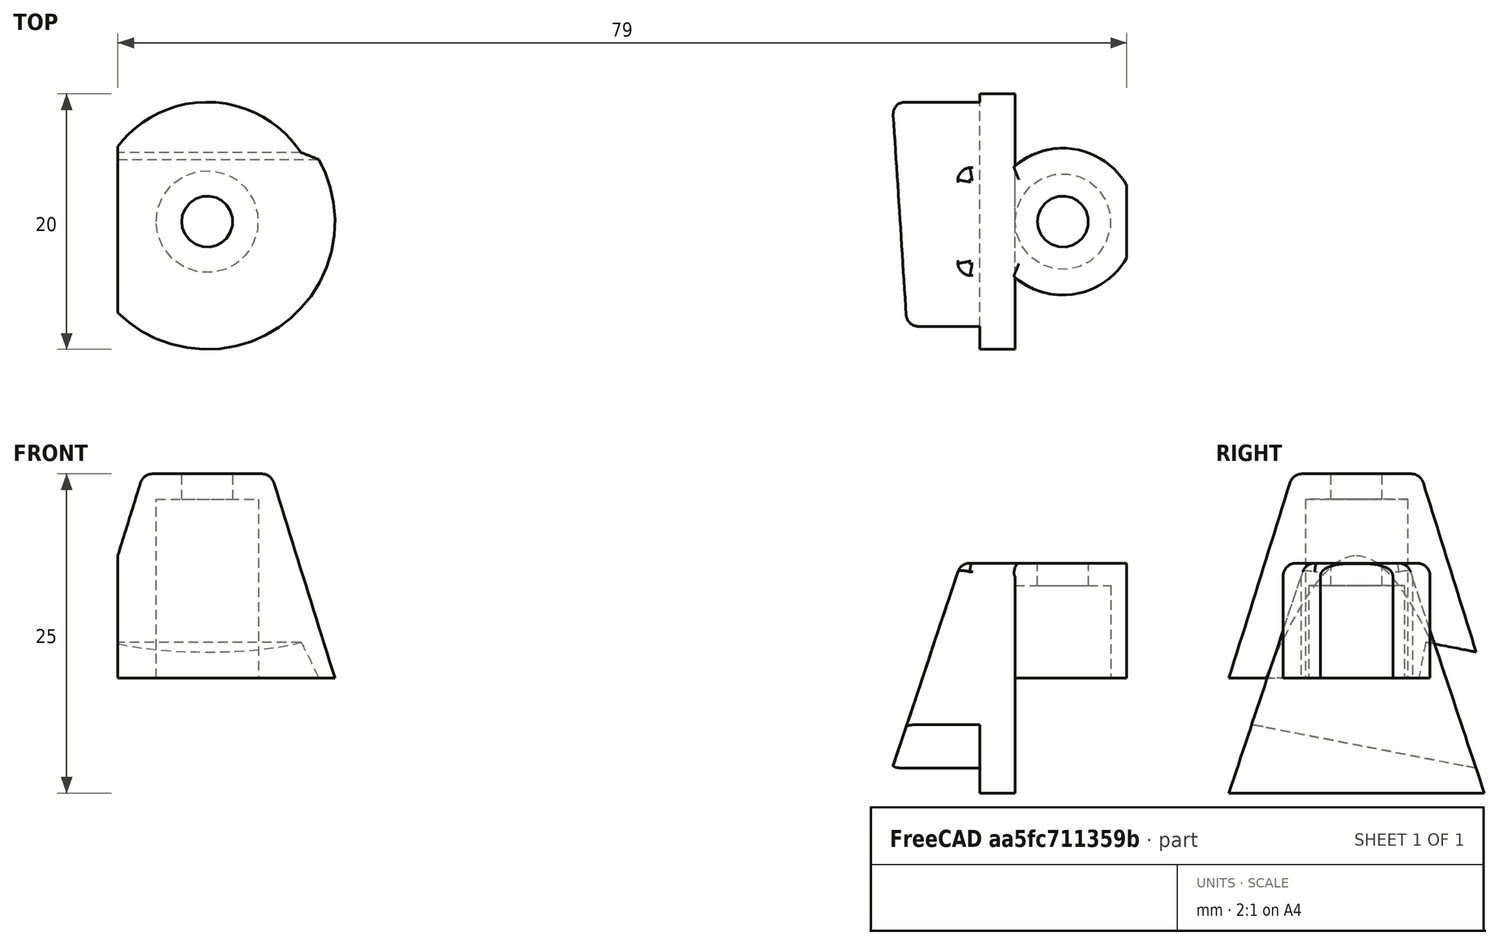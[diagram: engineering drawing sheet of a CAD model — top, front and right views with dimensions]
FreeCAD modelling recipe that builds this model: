
FCSTD DOCUMENT  (FreeCAD 0.21R33771 (Git))
Label: Decent800 brackets
License: All rights reserved
LicenseURL: http://en.wikipedia.org/wiki/All_rights_reserved
objects: PartDesign::SubtractiveCylinder×4, PartDesign::SubtractiveBox×4, PartDesign::Fillet×3, PartDesign::Body×2, Part::FeaturePython×2, PartDesign::AdditiveCylinder×1, PartDesign::AdditiveWedge×1, PartDesign::AdditiveCone×1, Spreadsheet::Sheet×1, PartDesign::Plane×1
note: 33 computed .brp shape members not serialized (recipe doc carries the construction recipe); baked Part::Feature solids carry a one-line shape summary decoded from their .brp

FEATURE [PartDesign::AdditiveCylinder] Cylinder
  Angle = 360
  AttacherType = Attacher::AttachEngine3D
  FirstAngle = 0
  Height = 9
  Radius = 5.75
  SecondAngle = 0
FEATURE [PartDesign::SubtractiveCylinder] Cylinder001
  Angle = 360
  AttacherType = Attacher::AttachEngine3D
  BaseFeature = -> Cylinder
  FirstAngle = 0
  Height = 9
  MapMode = 2
  Radius = 2
  SecondAngle = 0
  Support = -> [XY_Plane]
FEATURE [PartDesign::SubtractiveCylinder] Cylinder002
  Angle = 360
  AttacherType = Attacher::AttachEngine3D
  BaseFeature = -> Cylinder001
  FirstAngle = 0
  Height = 7.25
  MapMode = 5
  Radius = 3.75
  SecondAngle = 0
  Support = -> [XY_Plane]
FEATURE [PartDesign::AdditiveWedge] Wedge
  AttacherType = Attacher::AttachEngine3D
  BaseFeature = -> Cylinder002
  MapMode = 5
  Placement = pos=(0,0,0) rot=(0.57735,0.57735,0.57735;2.0944rad)
  Refine = true
  Support = -> [YZ_Plane]
  X2max = 4
  X2min = -4
  Xmax = 10
  Xmin = -10
  Ymax = 9
  Ymin = -9
  Z2max = 8
  Z2min = 3.75
  Zmax = 14
  Zmin = 3.75
FEATURE [PartDesign::SubtractiveBox] Box
  AttacherType = Attacher::AttachEngine3D
  AttachmentOffset = pos=(6.5,-15,-12.5) rot=(-1,0,0;0.191986rad)
  BaseFeature = -> Wedge
  Height = 10
  Length = 20
  MapMode = 5
  Placement = pos=(6.5,-15,-12.5) rot=(-1,0,0;0.191986rad)
  Support = -> [XY_Plane]
  Width = 30
  expr: .AttachmentOffset.Rotation.Angle = <<Spreadsheet>>.KeebAngle
FEATURE [PartDesign::Fillet] Fillet
  Base = -> Box [Edge8,Edge1]
  BaseFeature = -> Box
  Placement = pos=(6.5,-15,-12.5) rot=(-1,0,0;0.191986rad)
  Radius = 1
  SupportTransform = false
  UseAllEdges = false
FEATURE [PartDesign::Fillet] Fillet001
  Base = -> Fillet [Edge10,Edge9]
  BaseFeature = -> Fillet
  Placement = pos=(6.5,-15,-12.5) rot=(-1,0,0;0.191986rad)
  Radius = 1
  SupportTransform = false
  UseAllEdges = false
FEATURE [PartDesign::AdditiveCone] Cone
  Angle = 360
  AttacherType = Attacher::AttachEngine3D
  Height = 16
  MapMode = 5
  Radius1 = 10
  Radius2 = 5
  Support = -> [XY_Plane001]
FEATURE [PartDesign::SubtractiveCylinder] Cylinder003
  Angle = 360
  AttacherType = Attacher::AttachEngine3D
  BaseFeature = -> Cone
  FirstAngle = 0
  Height = 16
  MapMode = 2
  Radius = 2
  SecondAngle = 0
  Support = -> [Cylinder001]
FEATURE [PartDesign::SubtractiveCylinder] Cylinder004
  Angle = 360
  AttacherType = Attacher::AttachEngine3D
  BaseFeature = -> Cylinder003
  FirstAngle = 0
  Height = 14
  MapMode = 2
  Radius = 4
  SecondAngle = 0
  Support = -> [Cylinder002]
FEATURE [PartDesign::SubtractiveBox] Box001
  AttacherType = Attacher::AttachEngine3D
  AttachmentOffset = pos=(-15,3.5,-7) rot=(1,0,0;-0.191986rad)
  BaseFeature = -> Cylinder004
  Height = 10
  Length = 30
  MapMode = 5
  Placement = pos=(-15,3.5,-7) rot=(1,0,0;6.0912rad)
  Support = -> [XY_Plane001]
  Width = 10
  expr: .AttachmentOffset.Rotation.Angle = -<<Spreadsheet>>.KeebAngle
FEATURE [Spreadsheet::Sheet] Spreadsheet
  cells = A1='KeebAngle; B1(KeebAngle)=11
FEATURE [PartDesign::Fillet] Fillet002
  Base = -> Box001 [Edge7]
  BaseFeature = -> Box001
  Placement = pos=(-15,3.5,-7) rot=(-1,0,0;0.191986rad)
  Radius = 1
  SupportTransform = false
  UseAllEdges = false
FEATURE [PartDesign::SubtractiveBox] Box002
  AttacherType = Attacher::AttachEngine3D
  AttachmentOffset = pos=(7,-15,0) rot=(0,0,1;0rad)
  BaseFeature = -> Fillet002
  Height = 20
  Length = 10
  MapMode = 5
  Placement = pos=(7,-15,0) rot=(0,0,1;0rad)
  Support = -> [XY_Plane001]
  Width = 30
FEATURE [PartDesign::Body] Body001  label="ScrewColumn 3"
  Group = -> [Cone,Cylinder003,Cylinder004,Box001,Fillet002,Box002]
  Origin = -> Origin001
  Placement = pos=(-18,0,0) rot=(0,0,1;0rad)
  Tip = -> Box002
FEATURE [Part::FeaturePython] Clone001  label="ScrewColumn 4"  # Draft clone (typed FeaturePython)
  AttacherType = Attacher::AttachEngine3D
  Fuse = false
  Objects = -> [Body001]
  Placement = pos=(-40,0,0) rot=(0,0,1;0rad)
  Scale = (-1,1,1)
FEATURE [PartDesign::Plane] DatumPlane
  AttachmentOffset = pos=(0,0,-5) rot=(0,0,1;0rad)
  Length = 60
  MapMode = 4
  Placement = pos=(-5,0,1.1e-15) rot=(0.707107,0,0.707107;3.14159rad)
  ResizeMode = 0
  Support = -> [XZ_Plane]
  Width = 60
FEATURE [PartDesign::SubtractiveBox] Box003
  AttacherType = Attacher::AttachEngine3D
  AttachmentOffset = pos=(-10,-7.5,0) rot=(0,0,1;0rad)
  BaseFeature = -> Fillet001
  Height = 2
  Length = 10
  MapMode = 5
  Placement = pos=(-5,7.5,10) rot=(-0.707107,0,0.707107;3.14159rad)
  Support = -> [DatumPlane]
  Width = 15
FEATURE [PartDesign::Body] Body  label="ScrewColumn 1"
  Group = -> [Cylinder,Cylinder001,Cylinder002,Wedge,Box,Fillet,Fillet001,DatumPlane,Box003]
  Origin = -> Origin
  Tip = -> Box003
FEATURE [Part::FeaturePython] Clone  label="ScrewColumn 2"  # Draft clone (typed FeaturePython)
  AttacherType = Attacher::AttachEngine3D
  Fuse = false
  Objects = -> [Body]
  Placement = pos=(27,0,0) rot=(0,0,1;0rad)
  Scale = (-1,1,1)
